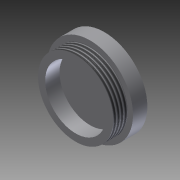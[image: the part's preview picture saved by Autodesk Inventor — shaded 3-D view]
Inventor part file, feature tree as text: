
AUTODESK INVENTOR PART (.ipt)
format: ipt  version: 2011 (Build 150239000, 239)  size: 96,256 bytes
history: native  units: in
note: dims shown in document units (in); Inventor stores cm internally (conversion verified against a paired STEP export)
features: extrude x3, sketch x3, thread x1
ambient origin geometry x8: Origin, YZ Plane, XZ Plane, XY Plane, X Axis, Y Axis, Z Axis, Center Point
bodies: Solid1 (feature_tree)
feature tree (7):
  extrude  "Extrusion1"  Depth=0.1in TaperAngle=0.0deg
  extrude  "Extrusion2"  Depth=0.1in TaperAngle=0.0deg
  thread  "Thread1"  [1 undecoded]
  extrude  "Extrusion3"  Depth=0.1in TaperAngle=0.0deg
  sketch  "Sketch1"  dims[d0=0.6in d1=0.1in d2=0.0in]
  sketch  "Sketch2"  dims[d3=0.525in d4=0.1in d5=0.0in d6=1.0in d7=0.0in]
  sketch  "Sketch3"  dims[d8=0.425in d9=0.1in d10=0.0in]
note: 1 required parameter value undecoded (feature->parameter linkage not recoverable at this tier; creation-order binding heuristic only, values carry confidence <= 0.55)
